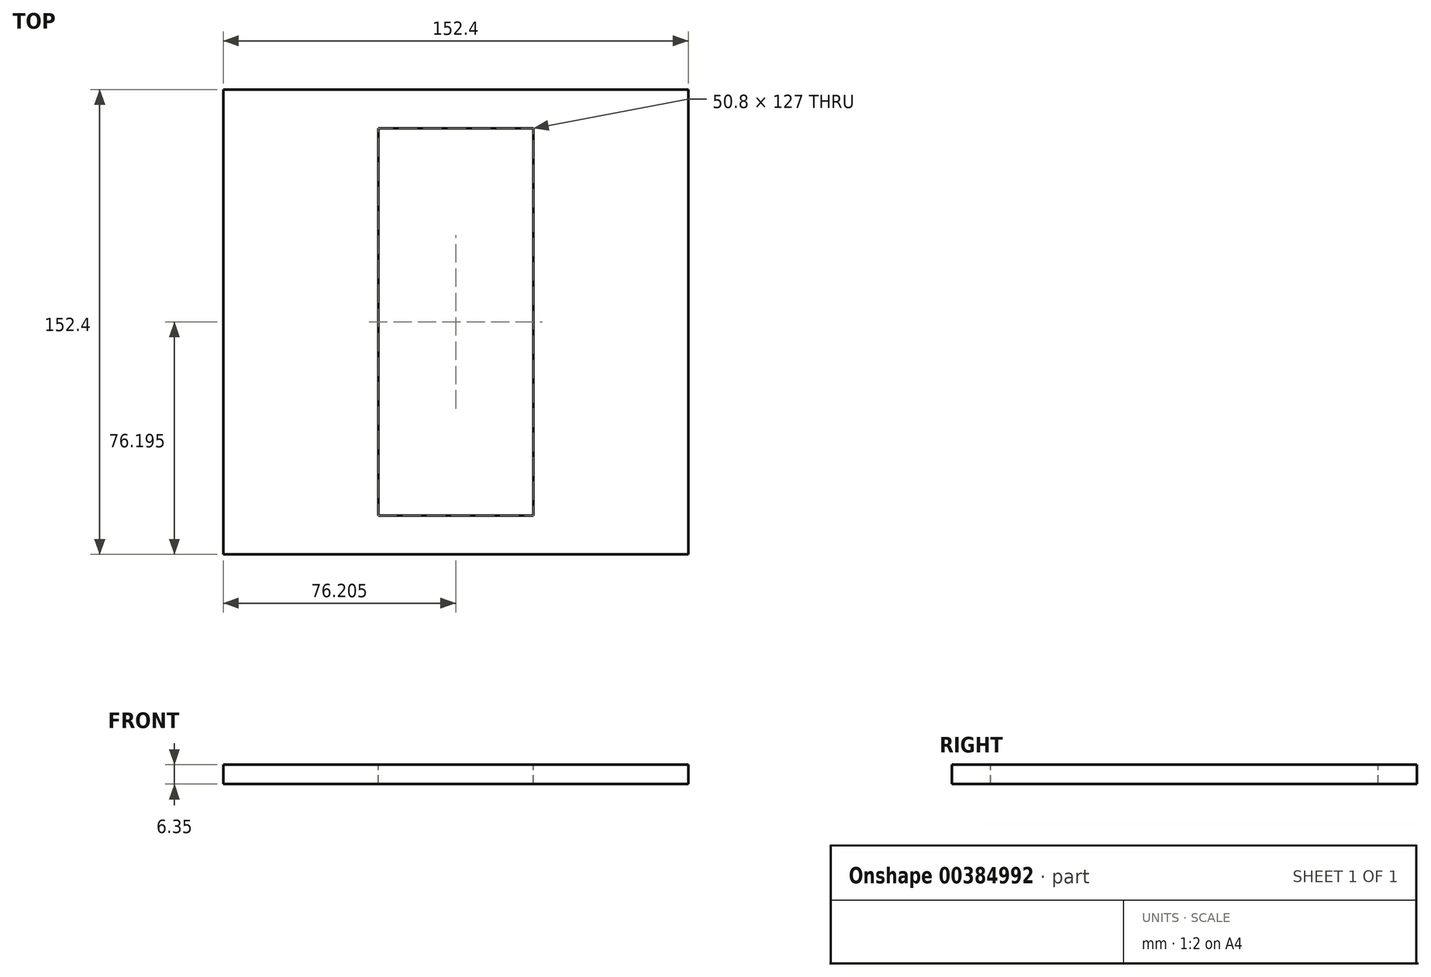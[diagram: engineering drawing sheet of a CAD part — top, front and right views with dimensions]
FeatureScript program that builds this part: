
annotation { "Feature Type Name" : "Feature", "Feature Type Description" : "" }
export const myFeature = defineFeature(function(context is Context, id is Id, definition is map)
    precondition{}
    {
        {
            var Q0;
            Q0=qCreatedBy(makeId("Top.planeOp"),FACE);
            var sketch = newSketch(context, id + "F0", { "sketchPlane" : qUnion([Q0])});
            skLineSegment(sketch, "E0.bottom", {"start": v(-81.93, 94.63) * mm, "end": v(70.47, 94.63) * mm});
            skLineSegment(sketch, "E0.top", {"start": v(-81.93, -57.77) * mm, "end": v(70.47, -57.77) * mm});
            skLineSegment(sketch, "E0.left", {"start": v(-81.93, 94.63) * mm, "end": v(-81.93, -57.77) * mm});
            skLineSegment(sketch, "E0.right", {"start": v(70.47, 94.63) * mm, "end": v(70.47, -57.77) * mm});
            skSolve(sketch);
        }
        {
            var Q0;
            Q0=makeQuery(id+"F0.imprint","IMPRINT",FACE,{"disambiguationData":[TD([[makeQuery(id+"F0.imprint","IMPRINT",EDGE,{"derivedFrom":sQuery(id+"F0.wireOp",EDGE,"E0.bottom")}),-1.0]])]});
            extrude(context, id + "F1", {"entities" : qUnion([Q0]), "depth" : 6.35 * mm, "offsetDistance" : 25.4 * mm});
        }
        {
            var Q0;
            Q0=makeQuery(id+"F1.opExtrude","CAP_FACE",FACE,{"disambiguationData":[OSD([sQuery(id+"F0.wireOp",EDGE,"E0.bottom"),sQuery(id+"F0.wireOp",EDGE,"E0.top"),sQuery(id+"F0.wireOp",EDGE,"E0.left"),sQuery(id+"F0.wireOp",EDGE,"E0.right")])],"isStart":false});
            var sketch = newSketch(context, id + "F2", { "sketchPlane" : qUnion([Q0])});
            skLineSegment(sketch, "E1.bottom", {"start": v(-31.13, 81.93) * mm, "end": v(19.67, 81.93) * mm});
            skLineSegment(sketch, "E1.top", {"start": v(-31.13, -45.07) * mm, "end": v(19.67, -45.07) * mm});
            skLineSegment(sketch, "E1.left", {"start": v(-31.13, 81.93) * mm, "end": v(-31.13, -45.07) * mm});
            skLineSegment(sketch, "E1.right", {"start": v(19.67, 81.93) * mm, "end": v(19.67, -45.07) * mm});
            skSolve(sketch);
        }
        {
            var Q0;
            Q0=makeQuery(id+"F2.imprint","IMPRINT",FACE,{"disambiguationData":[TD([[makeQuery(id+"F2.imprint","IMPRINT",EDGE,{"derivedFrom":sQuery(id+"F2.wireOp",EDGE,"E1.bottom")}),-1.0]])]});
            extrude(context, id + "F3", {"entities" : qUnion([Q0]), "operationType" : NewBodyOperationType.REMOVE, "oppositeDirection" : true, "depth" : 6.35 * mm, "offsetDistance" : 25.4 * mm});
        }
    });
